# Revit family: Foundation-Barrier-Stego-Wrap-Vapor_Barrier
name_source: partatom
category: Specialty Equipment
units: mm (PartAtom-declared; Revit-internal decimal feet)

## family parameters
Cut with Voids When Loaded = No
Host = Face
OmniClass Number = 23.25.05.21
OmniClass Title = Special Foundations
Part Type = Normal
Room Calculation Point = No
Round Connector Dimension = Use Diameter
Shared = No

## types (2) — shared parameters
ASTM = Exceeds ASTM E1745 Class A Requirements
BIMobject category = Waterproofing & Membranes
Brand url = http://www.stegoindustries.com
Date of publishing = 8/16/2017
Default Elevation = 0' - 0"
Design country = United States
Edition number = 1
Low Emitting Material = Yes
Manufacturer = Stego Industries, LLC
Manufacturer country = United States
Manufacturer name = Stego Industries, LLC
Masterformat 2014 Code = 07 26 00
Masterformat 2014 Description = Vapor Retarders
Material main = Polyethylene
Nominal height = 0' - 0"
Nominal width = 0' - 0"
Product Documentation Link = https://www.stegoindustries.com
Product Guid = 7ebc41d9-3dd5-4ce8-bf52-a3cebc659168
Product Page URL = https://www.stegoindustries.com
Product certification = https://www.stegoindustries.com
Product data url = https://bimobject.com
Product family = Thermal and Moisture Protective Products
Product group = Stego Wrap
QR code = http://bimobject.com
Stego Vapor Barrier = Stego® Wrap 15-mil Vapor Barrier
Technical description = Under-Slab Vapor Barrier
URL = http://www.stegoindustries.com
Weight Net (Kg) = 0
Youtube clip = https://www.youtube.com

## per-type parameters (varying)
| type | Description | Installation instructions | Max Length Note | Model | Product SKU | Product url | Vapor Barrier Thickness |
| Stego® Wrap Vapor Barrier 20 mils | Stego® Wrap 20-Mil Vapor Barrier is used as a below-slab vapor barrier and as a protection course for below grade waterproofing applications.  Stego's cutting-edge 20-Mil Vapor Barrier is developed from the same proprietary blend of prime virgin resins and additives as our popular 15-mil barrier, and provides additional protection for crucial projects.  This advanced multi-layer plastic extrusion blown film vapor barrier provides unrivaled moisture protection in even the most unforgiving conditions, such as intense fluctuating temperatures and humidity, and is frequently used on high-profile projects such as data centers and hospitals. | https://www.stegoindustries.com | Maximum roll length is 105'. | Stego® Wrap Vapor Barrier (20 mils) | stego006 | https://www.stegoindustries.com | 20 mils |
| Stego® Wrap Vapor Barrier 15 mils | Stego​® Wrap Vapor Barrier (15-mil) is a low permeance under-slab vapor barrier engineered to exceed ASTM E 1745  Class A Standards and provide long-term moisture vapor protection.  
Stego Wrap Vapor Barrier is a multi-layer plastic extrusion manufactured with only high grade prime, virgin, polyolefin resins. Stego Wrap Vapor Barrier can be used in systems for the control of soil gases (radon, methane), soil poisons (oil by-products) and sulfates. | https://www.stegoindustries.com
https://www.stegoindustries.com
https://www.stegoindustries.com | Maximum roll length is 140'. | Stego® Wrap Vapor Barrier (15 mils) | stego002 | https://www.stegoindustries.com
https://www.stegoindustries.com
https://www.stegoindustries.com | 15 mils |

## geometry (parser evidence)
native form markers: Sweep x2
no freeform markers — native parametric forms only
